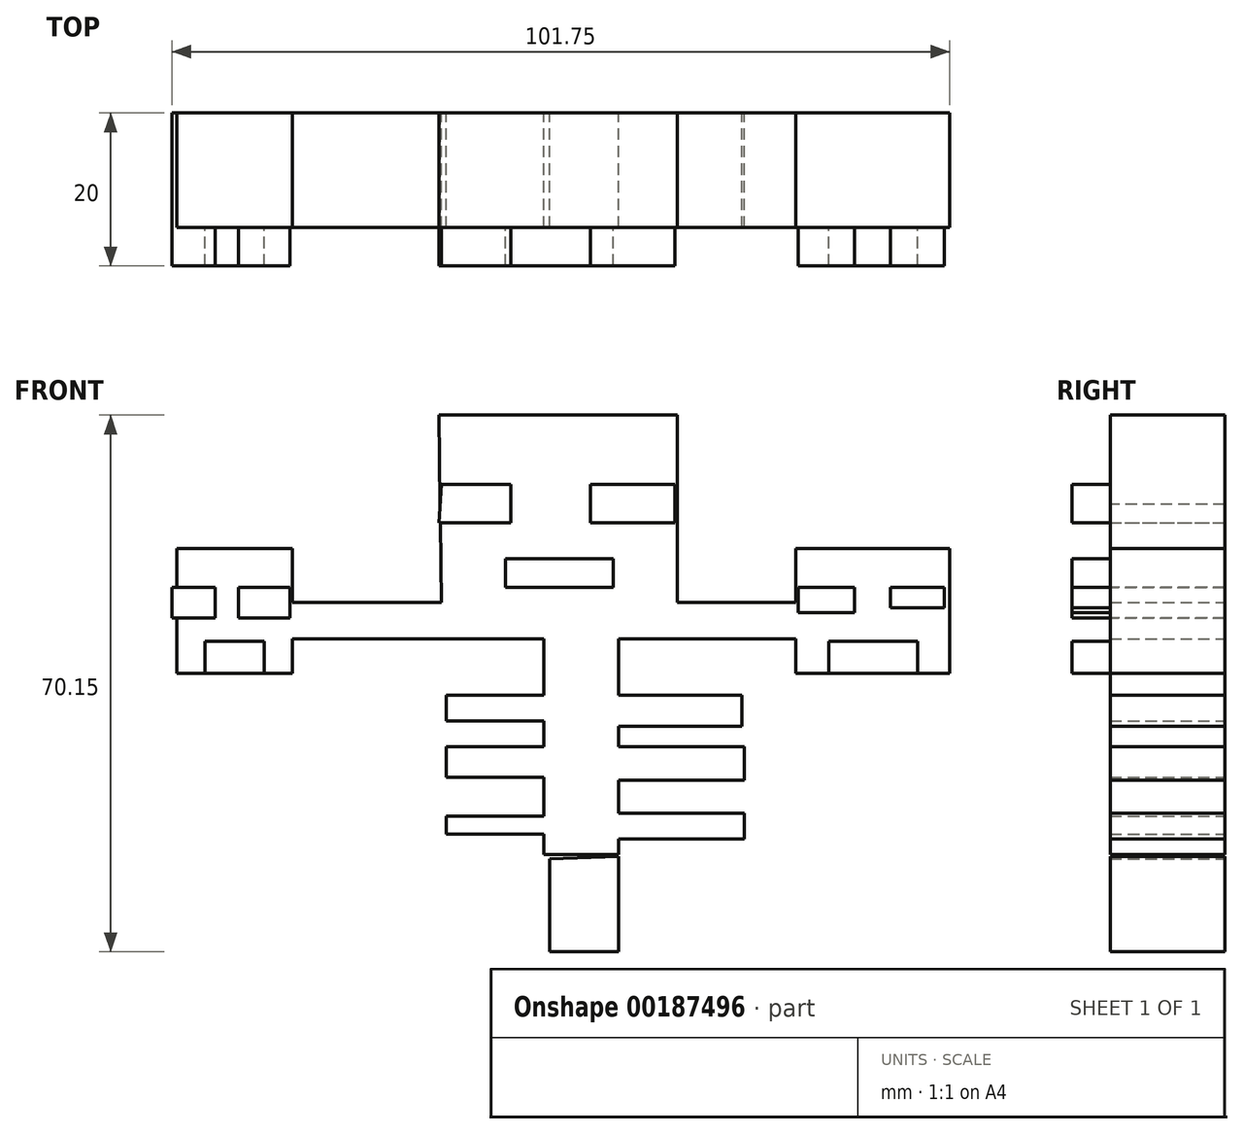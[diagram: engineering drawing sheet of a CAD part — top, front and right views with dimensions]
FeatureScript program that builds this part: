
annotation { "Feature Type Name" : "Feature", "Feature Type Description" : "" }
export const myFeature = defineFeature(function(context is Context, id is Id, definition is map)
    precondition{}
    {
        {
            var Q0;
            Q0=qCreatedBy(makeId("Front.planeOp"),FACE);
            var sketch = newSketch(context, id + "F0", { "sketchPlane" : qUnion([Q0])});
            skLineSegment(sketch, "E0", {"start": v(-19.48, 9.24) * mm, "end": v(8.4, 9.24) * mm});
            skLineSegment(sketch, "E1", {"start": v(-5.54, 9.24) * mm, "end": v(-38.96, 9.24) * mm});
            skLineSegment(sketch, "E2", {"start": v(-38.96, 9.24) * mm, "end": v(-38.96, 4.51) * mm});
            skLineSegment(sketch, "E3", {"start": v(-38.96, 4.51) * mm, "end": v(26.87, 4.51) * mm});
            skLineSegment(sketch, "E4", {"start": v(26.87, 4.51) * mm, "end": v(26.87, 9.24) * mm});
            skLineSegment(sketch, "E5", {"start": v(26.87, 9.24) * mm, "end": v(8.4, 9.24) * mm});
            skLineSegment(sketch, "E6", {"start": v(26.87, 9.24) * mm, "end": v(26.87, 0) * mm});
            skLineSegment(sketch, "E7", {"start": v(26.87, 0) * mm, "end": v(47.01, 0) * mm});
            skLineSegment(sketch, "E8", {"start": v(47.01, 0) * mm, "end": v(47.01, 16.27) * mm});
            skLineSegment(sketch, "E9", {"start": v(47.01, 16.27) * mm, "end": v(26.87, 16.27) * mm});
            skLineSegment(sketch, "E10", {"start": v(26.87, 16.27) * mm, "end": v(26.87, 4.51) * mm});
            skLineSegment(sketch, "E11", {"start": v(-38.96, 9.24) * mm, "end": v(-38.96, 16.27) * mm});
            skLineSegment(sketch, "E12", {"start": v(-38.96, 16.27) * mm, "end": v(-54.07, 16.27) * mm});
            skLineSegment(sketch, "E13", {"start": v(-54.07, 16.27) * mm, "end": v(-54.07, 0) * mm});
            skLineSegment(sketch, "E14", {"start": v(-54.07, 0) * mm, "end": v(-38.96, 0) * mm});
            skLineSegment(sketch, "E15", {"start": v(-38.96, 0) * mm, "end": v(-38.96, 4.51) * mm});
            skLineSegment(sketch, "E16", {"start": v(-6.04, 4.51) * mm, "end": v(-6.04, -23.71) * mm});
            skLineSegment(sketch, "E17", {"start": v(-6.04, -23.71) * mm, "end": v(3.7, -23.71) * mm});
            skLineSegment(sketch, "E18", {"start": v(3.7, -23.71) * mm, "end": v(3.7, 4.51) * mm});
            skLineSegment(sketch, "E19.bottom", {"start": v(3.7, -2.88) * mm, "end": v(19.81, -2.88) * mm});
            skLineSegment(sketch, "E19.top", {"start": v(3.7, -6.91) * mm, "end": v(19.81, -6.91) * mm});
            skLineSegment(sketch, "E19.left", {"start": v(3.7, -2.88) * mm, "end": v(3.7, -6.91) * mm});
            skLineSegment(sketch, "E19.right", {"start": v(19.81, -2.88) * mm, "end": v(19.81, -6.91) * mm});
            skLineSegment(sketch, "E20.bottom", {"start": v(3.7, -9.6) * mm, "end": v(20.15, -9.6) * mm});
            skLineSegment(sketch, "E20.top", {"start": v(3.7, -13.97) * mm, "end": v(20.15, -13.97) * mm});
            skLineSegment(sketch, "E20.left", {"start": v(3.7, -9.6) * mm, "end": v(3.7, -13.97) * mm});
            skLineSegment(sketch, "E20.right", {"start": v(20.15, -9.6) * mm, "end": v(20.15, -13.97) * mm});
            skLineSegment(sketch, "E21.bottom", {"start": v(3.7, -18.34) * mm, "end": v(20.15, -18.34) * mm});
            skLineSegment(sketch, "E21.top", {"start": v(3.7, -21.7) * mm, "end": v(20.15, -21.7) * mm});
            skLineSegment(sketch, "E21.left", {"start": v(3.7, -18.34) * mm, "end": v(3.7, -21.7) * mm});
            skLineSegment(sketch, "E21.right", {"start": v(20.15, -18.34) * mm, "end": v(20.15, -21.7) * mm});
            skLineSegment(sketch, "E22.bottom", {"start": v(-6.04, -2.88) * mm, "end": v(-18.8, -2.88) * mm});
            skLineSegment(sketch, "E22.top", {"start": v(-6.04, -6.24) * mm, "end": v(-18.8, -6.24) * mm});
            skLineSegment(sketch, "E22.left", {"start": v(-6.04, -2.88) * mm, "end": v(-6.04, -6.24) * mm});
            skLineSegment(sketch, "E22.right", {"start": v(-18.8, -2.88) * mm, "end": v(-18.8, -6.24) * mm});
            skLineSegment(sketch, "E23.bottom", {"start": v(-6.04, -9.6) * mm, "end": v(-18.8, -9.6) * mm});
            skLineSegment(sketch, "E23.top", {"start": v(-6.04, -13.63) * mm, "end": v(-18.8, -13.63) * mm});
            skLineSegment(sketch, "E23.left", {"start": v(-6.04, -9.6) * mm, "end": v(-6.04, -13.63) * mm});
            skLineSegment(sketch, "E23.right", {"start": v(-18.8, -9.6) * mm, "end": v(-18.8, -13.63) * mm});
            skLineSegment(sketch, "E24.bottom", {"start": v(-6.04, -21.02) * mm, "end": v(-18.8, -21.02) * mm});
            skLineSegment(sketch, "E24.top", {"start": v(-6.04, -18.67) * mm, "end": v(-18.8, -18.67) * mm});
            skLineSegment(sketch, "E24.left", {"start": v(-6.04, -21.02) * mm, "end": v(-6.04, -18.67) * mm});
            skLineSegment(sketch, "E24.right", {"start": v(-18.8, -21.02) * mm, "end": v(-18.8, -18.67) * mm});
            skLineSegment(sketch, "E25", {"start": v(11.42, 9.24) * mm, "end": v(11.42, 33.75) * mm});
            skLineSegment(sketch, "E26", {"start": v(11.42, 33.75) * mm, "end": v(-19.81, 33.75) * mm});
            skLineSegment(sketch, "E27", {"start": v(-19.81, 33.75) * mm, "end": v(-19.48, 9.24) * mm});
            skSolve(sketch);
        }
        {
            var Q0;
            Q0 = qSketchRegion(id + "F0", true);
            extrude(context, id + "F1", {"entities" : qUnion([Q0]), "depth" : 15 * mm});
        }
        {
            var Q0;
            Q0=qCreatedBy(makeId("Front.planeOp"),FACE);
            var sketch = newSketch(context, id + "F2", { "sketchPlane" : qUnion([Q0])});
            skLineSegment(sketch, "E28", {"start": v(-5.33, -24.25) * mm, "end": v(-5.33, -36.4) * mm});
            skLineSegment(sketch, "E29", {"start": v(-5.33, -36.4) * mm, "end": v(3.7, -36.4) * mm});
            skLineSegment(sketch, "E30", {"start": v(3.7, -36.4) * mm, "end": v(3.7, -23.97) * mm});
            skLineSegment(sketch, "E31", {"start": v(-5.33, -24.25) * mm, "end": v(3.7, -23.97) * mm});
            skSolve(sketch);
        }
        {
            var Q0;
            Q0 = qSketchRegion(id + "F2", true);
            extrude(context, id + "F3", {"entities" : qUnion([Q0]), "depth" : 15 * mm});
        }
        {
            var Q0;
            Q0=qCreatedBy(makeId("Front.planeOp"),FACE);
            var sketch = newSketch(context, id + "F4", { "sketchPlane" : qUnion([Q0])});
            skLineSegment(sketch, "E32", {"start": v(-19.48, 24.68) * mm, "end": v(-10.41, 24.68) * mm});
            skLineSegment(sketch, "E33", {"start": v(-10.41, 24.68) * mm, "end": v(-10.41, 19.65) * mm});
            skLineSegment(sketch, "E34", {"start": v(-10.41, 19.65) * mm, "end": v(-19.81, 19.65) * mm});
            skLineSegment(sketch, "E35", {"start": v(-19.81, 19.65) * mm, "end": v(-19.48, 24.68) * mm});
            skLineSegment(sketch, "E36", {"start": v(11.08, 24.68) * mm, "end": v(0, 24.68) * mm});
            skLineSegment(sketch, "E37", {"start": v(0, 24.68) * mm, "end": v(0, 19.65) * mm});
            skLineSegment(sketch, "E38", {"start": v(0, 19.65) * mm, "end": v(11.08, 19.65) * mm});
            skLineSegment(sketch, "E39", {"start": v(11.08, 19.65) * mm, "end": v(11.08, 24.68) * mm});
            skLineSegment(sketch, "E40.bottom", {"start": v(-11.08, 14.94) * mm, "end": v(3.02, 14.94) * mm});
            skLineSegment(sketch, "E40.top", {"start": v(-11.08, 11.25) * mm, "end": v(3.02, 11.25) * mm});
            skLineSegment(sketch, "E40.left", {"start": v(-11.08, 14.94) * mm, "end": v(-11.08, 11.25) * mm});
            skLineSegment(sketch, "E40.right", {"start": v(3.02, 14.94) * mm, "end": v(3.02, 11.25) * mm});
            skLineSegment(sketch, "E41.bottom", {"start": v(27.2, 11.25) * mm, "end": v(34.59, 11.25) * mm});
            skLineSegment(sketch, "E41.top", {"start": v(27.2, 7.9) * mm, "end": v(34.59, 7.9) * mm});
            skLineSegment(sketch, "E41.left", {"start": v(27.2, 11.25) * mm, "end": v(27.2, 7.9) * mm});
            skLineSegment(sketch, "E41.right", {"start": v(34.59, 11.25) * mm, "end": v(34.59, 7.9) * mm});
            skLineSegment(sketch, "E42.bottom", {"start": v(46.34, 11.25) * mm, "end": v(39.3, 11.25) * mm});
            skLineSegment(sketch, "E42.top", {"start": v(46.34, 8.56) * mm, "end": v(39.3, 8.56) * mm});
            skLineSegment(sketch, "E42.left", {"start": v(46.34, 11.25) * mm, "end": v(46.34, 8.56) * mm});
            skLineSegment(sketch, "E42.right", {"start": v(39.3, 11.25) * mm, "end": v(39.3, 8.56) * mm});
            skPoint(sketch, "E43.oppositeSnap0", {"position": v(42.82, 11.25) * mm});
            skLineSegment(sketch, "E43.bottom", {"start": v(31.23, 4.2) * mm, "end": v(42.82, 4.2) * mm});
            skLineSegment(sketch, "E43.top", {"start": v(31.23, 0) * mm, "end": v(42.82, 0) * mm});
            skLineSegment(sketch, "E43.left", {"start": v(31.23, 4.2) * mm, "end": v(31.23, 0) * mm});
            skLineSegment(sketch, "E43.right", {"start": v(42.82, 4.2) * mm, "end": v(42.82, 0) * mm});
            skLineSegment(sketch, "E44.bottom", {"start": v(-39.3, 11.25) * mm, "end": v(-46, 11.25) * mm});
            skLineSegment(sketch, "E44.top", {"start": v(-39.3, 7.22) * mm, "end": v(-46, 7.22) * mm});
            skLineSegment(sketch, "E44.left", {"start": v(-39.3, 11.25) * mm, "end": v(-39.3, 7.22) * mm});
            skLineSegment(sketch, "E44.right", {"start": v(-46, 11.25) * mm, "end": v(-46, 7.22) * mm});
            skLineSegment(sketch, "E45.bottom", {"start": v(-54.74, 11.25) * mm, "end": v(-49.03, 11.25) * mm});
            skLineSegment(sketch, "E45.top", {"start": v(-54.74, 7.22) * mm, "end": v(-49.03, 7.22) * mm});
            skLineSegment(sketch, "E45.left", {"start": v(-54.74, 11.25) * mm, "end": v(-54.74, 7.22) * mm});
            skLineSegment(sketch, "E45.right", {"start": v(-49.03, 11.25) * mm, "end": v(-49.03, 7.22) * mm});
            skPoint(sketch, "E46.oppositeSnap0", {"position": v(-42.65, 7.22) * mm});
            skLineSegment(sketch, "E46.bottom", {"start": v(-50.37, 0) * mm, "end": v(-42.65, 0) * mm});
            skLineSegment(sketch, "E46.top", {"start": v(-50.37, 4.2) * mm, "end": v(-42.65, 4.2) * mm});
            skLineSegment(sketch, "E46.left", {"start": v(-50.37, 0) * mm, "end": v(-50.37, 4.2) * mm});
            skLineSegment(sketch, "E46.right", {"start": v(-42.65, 0) * mm, "end": v(-42.65, 4.2) * mm});
            skSolve(sketch);
        }
        {
            var Q0;
            Q0 = qSketchRegion(id + "F4", true);
            extrude(context, id + "F5", {"entities" : qUnion([Q0]), "operationType" : NewBodyOperationType.ADD, "depth" : 20 * mm});
        }
    });
